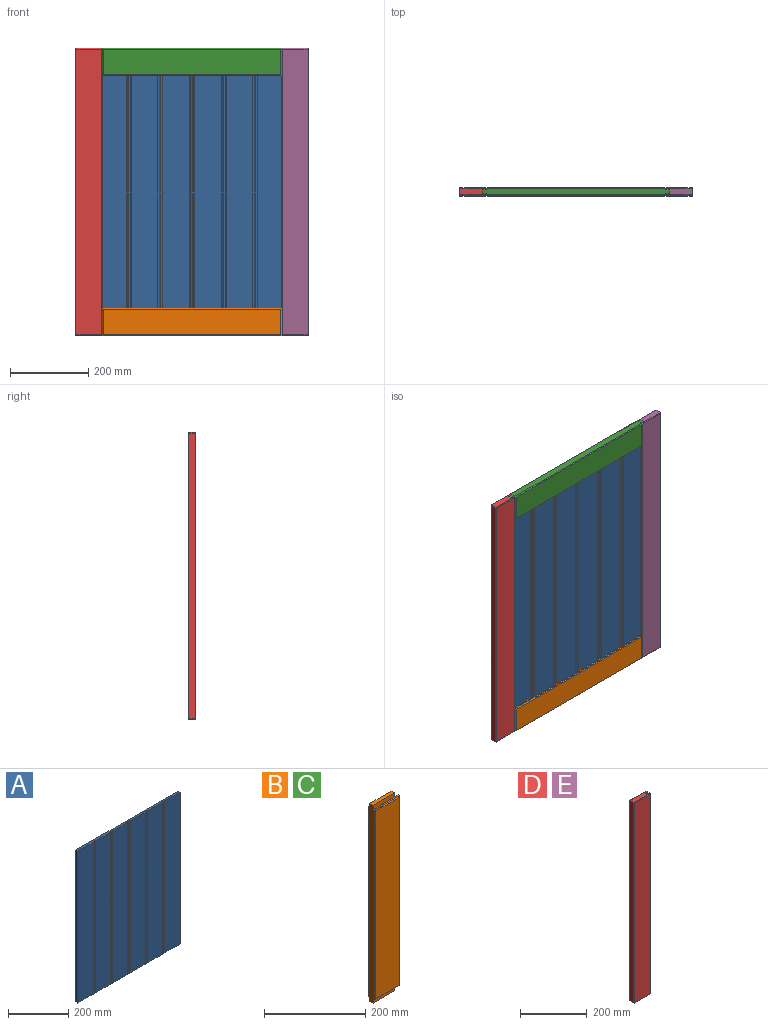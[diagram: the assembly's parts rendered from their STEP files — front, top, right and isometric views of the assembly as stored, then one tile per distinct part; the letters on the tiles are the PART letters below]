
ASSEMBLY  parts=5 mates=12
PART A: 41 faces, bbox 478x9x615 mm
  f0: plane 478x9mm, normal (0,0,1), area 4256.6mm2, adj f1,f2,f3,f4,f5,f6,f8,f9
  f1: plane 615x71mm, normal (0,-1,0), area 43665mm2, adj f0,f6,f7,f29
  f2: plane 615x69mm, normal (0,-1,0), area 42435mm2, adj f0,f7,f25,f28
  f3: plane 615x69mm, normal (0,-1,0), area 42435mm2, adj f0,f7,f21,f24
  f4: plane 615x69mm, normal (0,-1,0), area 42435mm2, adj f0,f7,f17,f20
  f5: plane 615x69mm, normal (0,-1,0), area 42435mm2, adj f0,f7,f13,f16
  f6: plane 615x9mm, normal (-1,0,0), area 5535mm2, adj f0,f1,f7,f10
  f7: plane 478x9mm, normal (0,0,-1), area 4256.6mm2, adj f1,f2,f3,f4,f5,f6,f8,f9
  f8: plane 615x9mm, normal (1,0,0), area 5535mm2, adj f0,f7,f9,f10
  f9: plane 615x71mm, normal (0,-1,0), area 43665mm2, adj f0,f7,f8,f12
  f10: plane 615x478mm, normal (0,1,0), area 293970mm2, adj f0,f6,f7,f8
  f11: plane 615x0.54mm, normal (0.71,-0.71,0), area 465.8mm2, adj f0,f7,f12,f32
  f12: plane 615x2mm, normal (-0.71,-0.71,0), area 1739.5mm2, adj f0,f7,f9,f11
  f13: plane 615x2mm, normal (0.71,-0.71,0), area 1739.5mm2, adj f0,f5,f7,f14
  f14: plane 615x0.54mm, normal (-0.71,-0.71,0), area 465.8mm2, adj f0,f7,f13,f31
  f15: plane 615x0.54mm, normal (0.71,-0.71,0), area 465.8mm2, adj f0,f7,f16,f34
  f16: plane 615x2mm, normal (-0.71,-0.71,0), area 1739.5mm2, adj f0,f5,f7,f15
  f17: plane 615x2mm, normal (0.71,-0.71,0), area 1739.5mm2, adj f0,f4,f7,f18
  f18: plane 615x0.54mm, normal (-0.71,-0.71,0), area 465.8mm2, adj f0,f7,f17,f33
  f19: plane 615x0.54mm, normal (0.71,-0.71,0), area 465.8mm2, adj f0,f7,f20,f36
  f20: plane 615x2mm, normal (-0.71,-0.71,0), area 1739.5mm2, adj f0,f4,f7,f19
  f21: plane 615x2mm, normal (0.71,-0.71,0), area 1739.5mm2, adj f0,f3,f7,f22
  f22: plane 615x0.54mm, normal (-0.71,-0.71,0), area 465.8mm2, adj f0,f7,f21,f35
  f23: plane 615x0.54mm, normal (0.71,-0.71,0), area 465.8mm2, adj f0,f7,f24,f38
  f24: plane 615x2mm, normal (-0.71,-0.71,0), area 1739.5mm2, adj f0,f3,f7,f23
  f25: plane 615x2mm, normal (0.71,-0.71,0), area 1739.5mm2, adj f0,f2,f7,f26
  f26: plane 615x0.54mm, normal (-0.71,-0.71,0), area 465.8mm2, adj f0,f7,f25,f37
  f27: plane 615x0.54mm, normal (0.71,-0.71,0), area 465.8mm2, adj f0,f7,f28,f40
  f28: plane 615x2mm, normal (-0.71,-0.71,0), area 1739.5mm2, adj f0,f2,f7,f27
  f29: plane 615x2mm, normal (0.71,-0.71,0), area 1739.5mm2, adj f0,f1,f7,f30
  f30: plane 615x0.54mm, normal (-0.71,-0.71,0), area 465.8mm2, adj f0,f7,f29,f39
  f31: cylinder r=5mm len=615mm, axis (0,0,1), area 2371.4mm2, adj f0,f7,f14,f32
  f32: cylinder r=5mm len=615mm, axis (0,0,1), area 2371.4mm2, adj f0,f7,f11,f31
  f33: cylinder r=5mm len=615mm, axis (0,0,1), area 2371.4mm2, adj f0,f7,f18,f34
  f34: cylinder r=5mm len=615mm, axis (0,0,1), area 2371.4mm2, adj f0,f7,f15,f33
  f35: cylinder r=5mm len=615mm, axis (0,0,1), area 2371.4mm2, adj f0,f7,f22,f36
  f36: cylinder r=5mm len=615mm, axis (0,0,1), area 2371.4mm2, adj f0,f7,f19,f35
  f37: cylinder r=5mm len=615mm, axis (0,0,1), area 2371.4mm2, adj f0,f7,f26,f38
  f38: cylinder r=5mm len=615mm, axis (0,0,1), area 2371.4mm2, adj f0,f7,f23,f37
  f39: cylinder r=5mm len=615mm, axis (0,0,1), area 2371.4mm2, adj f0,f7,f30,f40
  f40: cylinder r=5mm len=615mm, axis (0,0,1), area 2371.4mm2, adj f0,f7,f27,f39
PART B: 26 faces, bbox 70x20x478 mm
  f0: plane 478x16mm, normal (-1,0,0), area 7508mm2, adj f7,f8,f10,f11,f12,f13,f14,f15
  f1: plane 454x66mm, normal (0,-1,0), area 29964mm2, adj f18,f19,f20,f21
  f2: plane 458x3.5mm, normal (1,0,0), area 1603mm2, adj f3,f10,f17,f21
  f3: plane 458x10mm, normal (0,1,0), area 4580mm2, adj f2,f9,f10,f17
  f4: plane 458x10mm, normal (0,-1,0), area 4580mm2, adj f5,f9,f12,f15
  f5: plane 458x3.5mm, normal (1,0,0), area 1603mm2, adj f4,f12,f15,f22
  f6: plane 454x66mm, normal (0,1,0), area 29964mm2, adj f22,f23,f24,f25
  f7: plane 60x9mm, normal (0,0,1), area 540mm2, adj f0,f9,f14,f16
  f8: plane 60x9mm, normal (0,0,-1), area 540mm2, adj f0,f9,f11,f13
  f9: plane 478x9mm, normal (1,0,0), area 4302mm2, adj f3,f4,f7,f8,f11,f13,f14,f16
  f10: plane 70x3.5mm, normal (0,0,-1), area 245mm2, adj f0,f2,f3,f11,f20
  f11: plane 60x10mm, normal (0,-1,0), area 600mm2, adj f0,f8,f9,f10
  f12: plane 70x3.5mm, normal (0,0,-1), area 245mm2, adj f0,f4,f5,f13,f24
  f13: plane 60x10mm, normal (0,1,0), area 600mm2, adj f0,f8,f9,f12
  f14: plane 60x10mm, normal (0,1,0), area 600mm2, adj f0,f7,f9,f15
  f15: plane 70x3.5mm, normal (0,0,1), area 245mm2, adj f0,f4,f5,f14,f23
  f16: plane 60x10mm, normal (0,-1,0), area 600mm2, adj f0,f7,f9,f17
  f17: plane 70x3.5mm, normal (0,0,1), area 245mm2, adj f0,f2,f3,f16,f19
  f18: plane 458x2mm, normal (-0.71,-0.71,0), area 1289.8mm2, adj f0,f1,f19,f20
  f19: plane 70x2mm, normal (0,-0.71,0.71), area 192.3mm2, adj f1,f17,f18,f21
  f20: plane 70x2mm, normal (0,-0.71,-0.71), area 192.3mm2, adj f1,f10,f18,f21
  f21: plane 458x2mm, normal (0.71,-0.71,0), area 1289.8mm2, adj f1,f2,f19,f20
  f22: plane 458x2mm, normal (0.71,0.71,0), area 1289.8mm2, adj f5,f6,f23,f24
  f23: plane 70x2mm, normal (0,0.71,0.71), area 192.3mm2, adj f6,f15,f22,f25
  f24: plane 70x2mm, normal (0,0.71,-0.71), area 192.3mm2, adj f6,f12,f22,f25
  f25: plane 458x2mm, normal (-0.71,0.71,0), area 1289.8mm2, adj f0,f6,f23,f24
PART C: same geometry as B
PART D: 24 faces, bbox 70x20x735 mm
  f0: plane 731x16mm, normal (-1,0,0), area 11696mm2, adj f11,f18,f19,f23
  f1: plane 731x66mm, normal (0,-1,0), area 48246mm2, adj f10,f13,f17,f18
  f2: plane 735x3.5mm, normal (1,0,0), area 2572.5mm2, adj f3,f8,f9,f13
  f3: plane 735x10mm, normal (0,1,0), area 7350mm2, adj f2,f4,f8,f9
  f4: plane 735x9mm, normal (1,0,0), area 6615mm2, adj f3,f5,f8,f9
  f5: plane 735x10mm, normal (0,-1,0), area 7350mm2, adj f4,f6,f8,f9
  f6: plane 735x3.5mm, normal (1,0,0), area 2572.5mm2, adj f5,f8,f9,f16
  f7: plane 731x66mm, normal (0,1,0), area 48246mm2, adj f12,f16,f19,f20
  f8: plane 68x16mm, normal (0,0,1), area 998mm2, adj f2,f3,f4,f5,f6,f17,f20,f23
  f9: plane 68x16mm, normal (0,0,-1), area 998mm2, adj f2,f3,f4,f5,f6,f10,f11,f12
  f10: plane 68x2mm, normal (0,-0.71,-0.71), area 189.5mm2, adj f1,f9,f13,f14
  f11: plane 16x2mm, normal (-0.71,0,-0.71), area 45.3mm2, adj f0,f9,f14,f15
  f12: plane 68x2mm, normal (0,0.71,-0.71), area 189.5mm2, adj f7,f9,f15,f16
  f13: plane 735x2mm, normal (0.71,-0.71,0), area 2073.2mm2, adj f1,f2,f10,f17
  f14: plane 2x2mm, normal (-0.58,-0.58,-0.58), area 3.5mm2, adj f10,f11,f18
  f15: plane 2x2mm, normal (-0.58,0.58,-0.58), area 3.5mm2, adj f11,f12,f19
  f16: plane 735x2mm, normal (0.71,0.71,0), area 2073.2mm2, adj f6,f7,f12,f20
  f17: plane 68x2mm, normal (0,-0.71,0.71), area 189.5mm2, adj f1,f8,f13,f21
  f18: plane 731x2mm, normal (-0.71,-0.71,0), area 2067.6mm2, adj f0,f1,f14,f21
  f19: plane 731x2mm, normal (-0.71,0.71,0), area 2067.6mm2, adj f0,f7,f15,f22
  f20: plane 68x2mm, normal (0,0.71,0.71), area 189.5mm2, adj f7,f8,f16,f22
  f21: plane 2x2mm, normal (-0.58,-0.58,0.58), area 3.5mm2, adj f17,f18,f23
  f22: plane 2x2mm, normal (-0.58,0.58,0.58), area 3.5mm2, adj f19,f20,f23
  f23: plane 16x2mm, normal (-0.71,0,0.71), area 45.3mm2, adj f0,f8,f21,f22
PART E: same geometry as D
PLACE A t=(-1126.11,309.27,46.64)mm
PLACE B rot(axis=(0,-1,0),90deg) t=(-648.11,294.77,-13.36)mm
PLACE C rot(axis=(0,1,0),90deg) t=(-1126.11,294.77,721.64)mm
PLACE D rot(axis=(1,0,0),180deg) t=(-1186.11,314.77,721.64)mm
PLACE E rot(axis=(0,1,0),180deg) t=(-588.11,294.77,721.64)mm
MATE planar A.f10 <-> B.f4  axis (0,1,0) through (-887.11,309.27,354.14)mm
MATE planar C.f12 <-> D.f6  axis (-1,0,0) through (-1116.11,311.02,686.64)mm
MATE planar C.f0 <-> E.f9  axis (0,0,1) through (-887.11,304.77,721.64)mm
MATE planar D.f2 <-> B.f17  axis (1,0,0) through (-1116.11,311.02,354.14)mm
MATE planar B.f0 <-> D.f8  axis (0,0,-1) through (-887.11,304.77,-13.36)mm
MATE planar A.f6 <-> D.f4  axis (-1,0,0) through (-1126.11,304.77,354.14)mm
MATE planar C.f17 <-> E.f2  axis (1,0,0) through (-658.11,298.52,686.64)mm
MATE planar B.f1 <-> D.f7  axis (0,-1,0) through (-887.11,294.77,21.64)mm
MATE planar A.f7 <-> B.f9  axis (0,0,-1) through (-887.11,304.81,46.64)mm
MATE planar C.f1 <-> D.f7  axis (0,-1,0) through (-887.11,294.77,686.64)mm
MATE planar E.f1 <-> B.f1  axis (0,-1,0) through (-623.11,294.77,354.14)mm
MATE planar C.f0 <-> D.f9  axis (0,0,1) through (-887.11,304.77,721.64)mm
